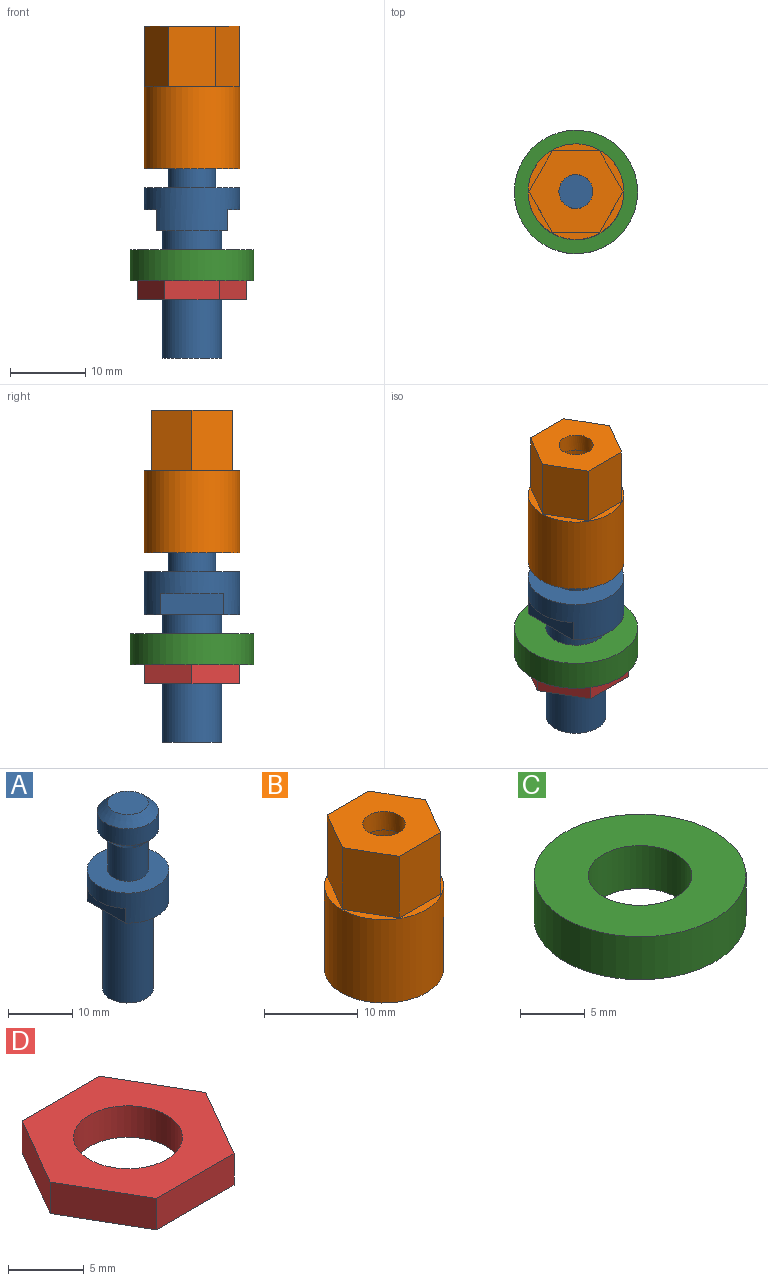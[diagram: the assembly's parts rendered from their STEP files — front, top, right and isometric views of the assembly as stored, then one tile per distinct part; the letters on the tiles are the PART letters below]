
ASSEMBLY  parts=4 mates=5
PART A: 14 faces, bbox 12.7x12.7x35.3 mm
  f0: plane 12.7x9.53mm, normal (0,0,-1), area 58.9mm2, adj f3,f4,f8,f10
  f1: plane 6.35x6.35mm, normal (0,0,1), area 31.7mm2, adj f13
  f2: plane 7.94x7.94mm, normal (0,0,-1), area 49.5mm2, adj f3
  f3: cylinder r=3.97mm len=16.89mm, axis (0,0,-1), area 421.2mm2, adj f0,f2
  f4: cylinder r=6.35mm len=12.7mm, axis (0,0,-1), area 176.7mm2, adj f0,f5,f8,f9,f10,f11
  f5: plane 12.7x12.7mm, normal (0,0,1), area 95mm2, adj f4,f6
  f6: cylinder r=3.17mm len=6.35mm, axis (0,0,-1), area 126.7mm2, adj f5,f12
  f7: cylinder r=4.76mm len=9.53mm, axis (0,0,-1), area 95mm2, adj f12,f13
  f8: plane 8.4x2.79mm, normal (1,0,0), area 23.5mm2, adj f0,f4,f9
  f9: plane 8.4x1.59mm, normal (0,0,-1), area 9.1mm2, adj f4,f8
  f10: plane 8.4x2.79mm, normal (-1,0,0), area 23.5mm2, adj f0,f4,f11
  f11: plane 8.4x1.59mm, normal (0,0,-1), area 9.1mm2, adj f4,f10
  f12: cone r=3.17mm half-angle=45deg, axis (0,0,1), area 56mm2, adj f6,f7
  f13: cone r=4.76mm half-angle=45deg, axis (0,0,-1), area 56mm2, adj f1,f7
PART B: 13 faces, bbox 12.7x12.7x18.9 mm
  f0: cylinder r=2.26mm len=4.52mm, axis (0,0,-1), area 34.3mm2, adj f7,f12
  f1: plane 8.05x6.25mm, normal (0,-1,0), area 50.3mm2, adj f2,f6,f7,f8
  f2: plane 8.05x5.41mm, normal (0.87,-0.5,0), area 50.3mm2, adj f1,f3,f7,f8
  f3: plane 8.05x5.41mm, normal (0.87,0.5,0), area 50.3mm2, adj f2,f4,f7,f8
  f4: plane 8.05x6.25mm, normal (0,1,0), area 50.3mm2, adj f3,f5,f7,f8
  f5: plane 8.05x5.41mm, normal (-0.87,0.5,0), area 50.3mm2, adj f4,f6,f7,f8
  f6: plane 8.05x5.41mm, normal (-0.87,-0.5,0), area 50.3mm2, adj f1,f5,f7,f8
  f7: plane 12.5x10.82mm, normal (0,0,1), area 85.4mm2, adj f0,f1,f2,f3,f4,f5,f6
  f8: plane 12.7x12.7mm, normal (0,0,1), area 25.2mm2, adj f1,f2,f3,f4,f5,f6,f10
  f9: plane 12.7x12.7mm, normal (0,0,-1), area 68.4mm2, adj f10,f11
  f10: cylinder r=6.35mm len=12.7mm, axis (0,0,1), area 433.7mm2, adj f8,f9
  f11: cylinder r=4.31mm len=16.51mm, axis (0,0,-1), area 446.6mm2, adj f9,f12
  f12: plane 8.61x8.61mm, normal (0,0,-1), area 42.2mm2, adj f0,f11
PART C: 4 faces, bbox 16.4x16.4x4.1 mm
  f0: cylinder r=4mm len=8mm, axis (0,0,-1), area 102.2mm2, adj f2,f3
  f1: cylinder r=8.19mm len=16.38mm, axis (0,0,-1), area 209.2mm2, adj f2,f3
  f2: plane 16.38x16.38mm, normal (0,0,1), area 160.5mm2, adj f0,f1
  f3: plane 16.38x16.38mm, normal (0,0,-1), area 160.5mm2, adj f0,f1
PART D: 9 faces, bbox 14.5x12.5x2.5 mm
  f0: plane 7.24x2.54mm, normal (0,-1,0), area 18.4mm2, adj f1,f6,f7,f8
  f1: plane 6.27x3.62mm, normal (0.87,-0.5,0), area 18.4mm2, adj f0,f2,f7,f8
  f2: plane 6.27x3.62mm, normal (0.87,0.5,0), area 18.4mm2, adj f1,f3,f7,f8
  f3: plane 7.24x2.54mm, normal (0,1,0), area 18.4mm2, adj f2,f4,f7,f8
  f4: plane 6.27x3.62mm, normal (-0.87,0.5,0), area 18.4mm2, adj f3,f6,f7,f8
  f5: cylinder r=3.59mm len=7.19mm, axis (0,0,-1), area 57.4mm2, adj f7,f8
  f6: plane 6.27x3.62mm, normal (-0.87,-0.5,0), area 18.4mm2, adj f0,f4,f7,f8
  f7: plane 14.48x12.54mm, normal (0,0,1), area 95.6mm2, adj f0,f1,f2,f3,f4,f5,f6
  f8: plane 14.48x12.54mm, normal (0,0,-1), area 95.6mm2, adj f0,f1,f2,f3,f4,f5,f6
PLACE A t=(-16.39,-0.43,29.75)mm fixed
PLACE B t=(-16.39,-0.43,36.81)mm
PLACE C t=(-16.39,-0.43,11.08)mm
PLACE D t=(-16.39,-0.43,8.54)mm
MATE fastened D.f5 <-> C.f0  axis (0,0,1) through (-16.39,-0.43,11.08)mm
MATE cylindrical B.f11 <-> A.f3  axis (0,0,-1) through (-16.39,-0.43,25.94)mm
MATE slider D.f5 <-> C.f0  axis (0,0,-1) through (-16.39,-0.43,11.08)mm
MATE slider A.f3 <-> C.f1  axis (0,0,-1) through (-16.39,-0.43,17.68)mm
MATE fastened B.f10 <-> A.f3  axis (0,0,-1) through (-16.39,-0.43,25.94)mm
